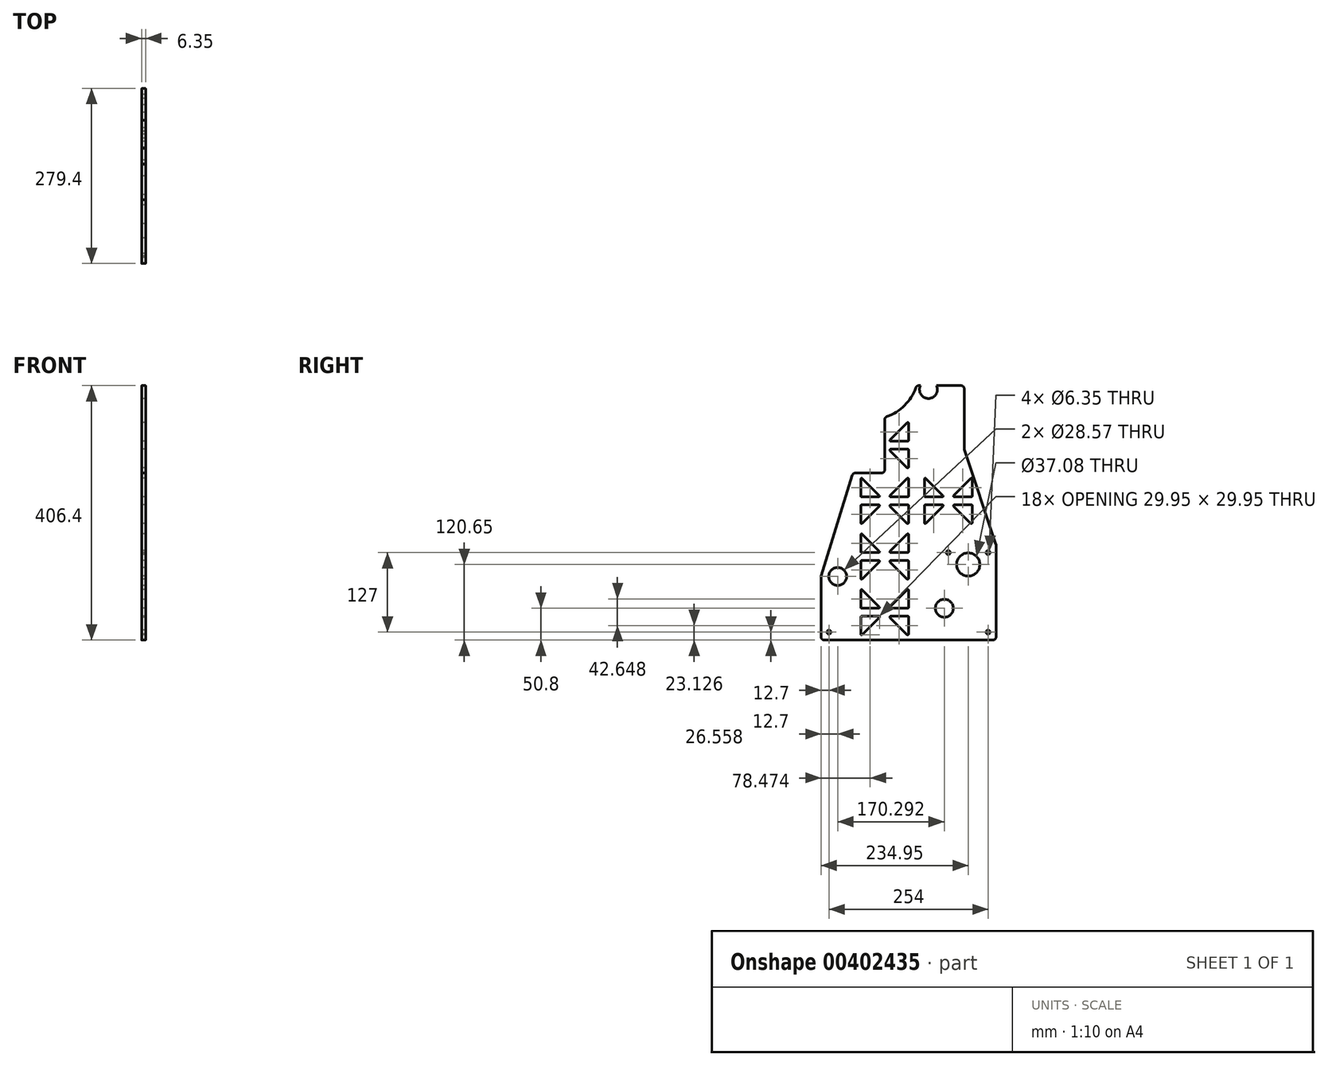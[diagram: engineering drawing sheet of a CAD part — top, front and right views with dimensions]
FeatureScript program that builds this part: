
annotation { "Feature Type Name" : "Feature", "Feature Type Description" : "" }
export const myFeature = defineFeature(function(context is Context, id is Id, definition is map)
    precondition{}
    {
        {
            var Q0;
            Q0=qCreatedBy(makeId("Right.planeOp"),FACE);
            var sketch = newSketch(context, id + "F0", { "sketchPlane" : qUnion([Q0])});
            skLineSegment(sketch, "E0.bottom", {"start": v(0, 0) * mm, "end": v(101.6, 0) * mm});
            skLineSegment(sketch, "E0.top", {"start": v(0, 406.4) * mm, "end": v(101.6, 406.4) * mm});
            skLineSegment(sketch, "E0.left", {"start": v(0, 0) * mm, "end": v(0, 406.4) * mm});
            skLineSegment(sketch, "E0.right", {"start": v(101.6, 0) * mm, "end": v(101.6, 406.4) * mm});
            skLineSegment(sketch, "E1.bottom", {"start": v(101.6, 0) * mm, "end": v(228.6, 0) * mm});
            skLineSegment(sketch, "E1.top", {"start": v(101.6, 152.4) * mm, "end": v(228.6, 152.4) * mm});
            skLineSegment(sketch, "E1.left", {"start": v(101.6, 0) * mm, "end": v(101.6, 152.4) * mm});
            skLineSegment(sketch, "E1.right", {"start": v(228.6, 0) * mm, "end": v(228.6, 152.4) * mm});
            skCircle(sketch, "E2", {"center": v(146.05, 50.8) * mm, "radius": 14.29 * mm});
            skCircle(sketch, "E3", {"center": v(146.05, 50.8) * mm, "radius": 50.8 * mm, "construction": true});
            skCircle(sketch, "E4", {"center": v(184.15, 120.65) * mm, "radius": 18.54 * mm});
            skCircle(sketch, "E5", {"center": v(215.9, 12.7) * mm, "radius": 3.18 * mm});
            skCircle(sketch, "E6", {"center": v(215.9, 139.7) * mm, "radius": 3.18 * mm});
            skPoint(sketch, "E7.startSnap0", {"position": v(50.8, 406.4) * mm});
            skLineSegment(sketch, "E8", {"start": v(50.8, 406.4) * mm, "end": v(50.8, -18.77) * mm, "construction": true});
            skPoint(sketch, "E8.endSnap0", {"position": v(50.8, 0) * mm});
            skArc(sketch, "E9.MirrorCS", {"start": v(12.7, 392.43) * mm, "mid": v(13.07, 393.33) * mm, "end": v(13.97, 393.7) * mm});
            skArc(sketch, "E10.MirrorCS", {"start": v(41.38, 393.7) * mm, "mid": v(42.56, 392.92) * mm, "end": v(42.28, 391.53) * mm});
            skPoint(sketch, "E11.MirrorP", {"position": v(12.7, 361.95) * mm});
            skLineSegment(sketch, "E12.MirrorCS", {"start": v(13.97, 393.7) * mm, "end": v(41.38, 393.7) * mm});
            skPoint(sketch, "E13.MirrorP", {"position": v(12.7, 393.7) * mm});
            skLineSegment(sketch, "E14.MirrorCS", {"start": v(42.28, 391.53) * mm, "end": v(14.87, 364.12) * mm});
            skPoint(sketch, "E15.MirrorP", {"position": v(44.45, 393.7) * mm});
            skArc(sketch, "E16.MirrorCS", {"start": v(14.87, 364.12) * mm, "mid": v(13.48, 363.84) * mm, "end": v(12.7, 365.02) * mm});
            skLineSegment(sketch, "E17.MirrorCS", {"start": v(12.7, 365.02) * mm, "end": v(12.7, 392.43) * mm});
            skLineSegment(sketch, "E18", {"start": v(-14.42, 355.6) * mm, "end": v(137.53, 355.6) * mm, "construction": true});
            skArc(sketch, "E19.MirrorCS", {"start": v(12.7, 318.77) * mm, "mid": v(13.07, 317.87) * mm, "end": v(13.97, 317.5) * mm});
            skArc(sketch, "E20.MirrorCS", {"start": v(60.22, 317.5) * mm, "mid": v(59.04, 318.28) * mm, "end": v(59.32, 319.67) * mm});
            skArc(sketch, "E21.MirrorCS", {"start": v(14.87, 347.08) * mm, "mid": v(13.48, 347.36) * mm, "end": v(12.7, 346.18) * mm});
            skArc(sketch, "E22.MirrorCS", {"start": v(41.38, 317.5) * mm, "mid": v(42.56, 318.28) * mm, "end": v(42.28, 319.67) * mm});
            skArc(sketch, "E23.MirrorCS", {"start": v(86.73, 347.08) * mm, "mid": v(88.12, 347.36) * mm, "end": v(88.9, 346.18) * mm});
            skArc(sketch, "E24.MirrorCS", {"start": v(88.9, 318.77) * mm, "mid": v(88.53, 317.87) * mm, "end": v(87.63, 317.5) * mm});
            skPoint(sketch, "E25.MirrorP", {"position": v(12.7, 349.25) * mm});
            skPoint(sketch, "E26.MirrorP", {"position": v(88.9, 349.25) * mm});
            skPoint(sketch, "E27.MirrorP", {"position": v(12.7, 317.5) * mm});
            skPoint(sketch, "E28.MirrorP", {"position": v(44.45, 317.5) * mm});
            skLineSegment(sketch, "E29.MirrorCS", {"start": v(50.8, 304.8) * mm, "end": v(50.8, 729.97) * mm, "construction": true});
            skPoint(sketch, "E30.MirrorP", {"position": v(88.9, 317.5) * mm});
            skLineSegment(sketch, "E31.MirrorCS", {"start": v(12.7, 346.18) * mm, "end": v(12.7, 318.77) * mm});
            skLineSegment(sketch, "E32.MirrorCS", {"start": v(88.9, 346.18) * mm, "end": v(88.9, 318.77) * mm});
            skLineSegment(sketch, "E33.MirrorCS", {"start": v(42.28, 319.67) * mm, "end": v(14.87, 347.08) * mm});
            skLineSegment(sketch, "E34.MirrorCS", {"start": v(13.97, 317.5) * mm, "end": v(41.38, 317.5) * mm});
            skPoint(sketch, "E35.MirrorP", {"position": v(57.15, 317.5) * mm});
            skLineSegment(sketch, "E36.MirrorCS", {"start": v(87.63, 317.5) * mm, "end": v(60.22, 317.5) * mm});
            skLineSegment(sketch, "E37.MirrorCS", {"start": v(59.32, 319.67) * mm, "end": v(86.73, 347.08) * mm});
            skPoint(sketch, "E38.0.1.0", {"position": v(44.45, 304.8) * mm});
            skLineSegment(sketch, "E38.0.1.1", {"start": v(12.7, 276.12) * mm, "end": v(12.7, 303.53) * mm});
            skPoint(sketch, "E38.0.1.2", {"position": v(12.7, 273.05) * mm});
            skPoint(sketch, "E38.0.1.3", {"position": v(12.7, 304.8) * mm});
            skLineSegment(sketch, "E38.0.1.4", {"start": v(42.28, 302.63) * mm, "end": v(14.87, 275.22) * mm});
            skLineSegment(sketch, "E38.0.1.5", {"start": v(13.97, 304.8) * mm, "end": v(41.38, 304.8) * mm});
            skPoint(sketch, "E38.0.1.6", {"position": v(12.7, 273.05) * mm});
            skArc(sketch, "E38.0.1.7", {"start": v(14.87, 275.22) * mm, "mid": v(13.48, 274.94) * mm, "end": v(12.7, 276.12) * mm});
            skArc(sketch, "E38.0.1.8", {"start": v(41.38, 304.8) * mm, "mid": v(42.56, 304.02) * mm, "end": v(42.28, 302.63) * mm});
            skArc(sketch, "E38.0.1.9", {"start": v(12.7, 303.53) * mm, "mid": v(13.07, 304.43) * mm, "end": v(13.97, 304.8) * mm});
            skPoint(sketch, "E38.0.1.10", {"position": v(44.45, 228.6) * mm});
            skLineSegment(sketch, "E38.0.1.11", {"start": v(13.97, 228.6) * mm, "end": v(41.38, 228.6) * mm});
            skPoint(sketch, "E38.0.1.12", {"position": v(12.7, 260.35) * mm});
            skLineSegment(sketch, "E38.0.1.13", {"start": v(42.28, 230.77) * mm, "end": v(14.87, 258.18) * mm});
            skPoint(sketch, "E38.0.1.14", {"position": v(12.7, 228.6) * mm});
            skLineSegment(sketch, "E38.0.1.15", {"start": v(12.7, 257.28) * mm, "end": v(12.7, 229.87) * mm});
            skPoint(sketch, "E38.0.1.16", {"position": v(12.7, 260.35) * mm});
            skArc(sketch, "E38.0.1.17", {"start": v(41.38, 228.6) * mm, "mid": v(42.56, 229.38) * mm, "end": v(42.28, 230.77) * mm});
            skArc(sketch, "E38.0.1.18", {"start": v(14.87, 258.18) * mm, "mid": v(13.48, 258.46) * mm, "end": v(12.7, 257.28) * mm});
            skArc(sketch, "E38.0.1.19", {"start": v(12.7, 229.87) * mm, "mid": v(13.07, 228.97) * mm, "end": v(13.97, 228.6) * mm});
            skPoint(sketch, "E38.0.1.20", {"position": v(57.15, 228.6) * mm});
            skPoint(sketch, "E38.0.1.21", {"position": v(88.9, 228.6) * mm});
            skLineSegment(sketch, "E38.0.1.22", {"start": v(59.32, 230.77) * mm, "end": v(86.73, 258.18) * mm});
            skLineSegment(sketch, "E38.0.1.23", {"start": v(87.63, 228.6) * mm, "end": v(60.22, 228.6) * mm});
            skPoint(sketch, "E38.0.1.24", {"position": v(88.9, 260.35) * mm});
            skLineSegment(sketch, "E38.0.1.25", {"start": v(88.9, 257.28) * mm, "end": v(88.9, 229.87) * mm});
            skPoint(sketch, "E38.0.1.26", {"position": v(88.9, 260.35) * mm});
            skArc(sketch, "E38.0.1.27", {"start": v(60.22, 228.6) * mm, "mid": v(59.04, 229.38) * mm, "end": v(59.32, 230.77) * mm});
            skArc(sketch, "E38.0.1.28", {"start": v(88.9, 229.87) * mm, "mid": v(88.53, 228.97) * mm, "end": v(87.63, 228.6) * mm});
            skArc(sketch, "E38.0.1.29", {"start": v(86.73, 258.18) * mm, "mid": v(88.12, 258.46) * mm, "end": v(88.9, 257.28) * mm});
            skLineSegment(sketch, "E38.0.1.30", {"start": v(88.9, 276.12) * mm, "end": v(88.9, 303.53) * mm});
            skLineSegment(sketch, "E38.0.1.31", {"start": v(59.32, 302.63) * mm, "end": v(86.73, 275.22) * mm});
            skLineSegment(sketch, "E38.0.1.32", {"start": v(87.63, 304.8) * mm, "end": v(60.22, 304.8) * mm});
            skPoint(sketch, "E38.0.1.33", {"position": v(88.9, 304.8) * mm});
            skPoint(sketch, "E38.0.1.34", {"position": v(88.9, 273.05) * mm});
            skPoint(sketch, "E38.0.1.35", {"position": v(57.15, 304.8) * mm});
            skPoint(sketch, "E38.0.1.36", {"position": v(88.9, 273.05) * mm});
            skArc(sketch, "E38.0.1.37", {"start": v(86.73, 275.22) * mm, "mid": v(88.12, 274.94) * mm, "end": v(88.9, 276.12) * mm});
            skArc(sketch, "E38.0.1.38", {"start": v(88.9, 303.53) * mm, "mid": v(88.53, 304.43) * mm, "end": v(87.63, 304.8) * mm});
            skArc(sketch, "E38.0.1.39", {"start": v(60.22, 304.8) * mm, "mid": v(59.04, 304.02) * mm, "end": v(59.32, 302.63) * mm});
            skPoint(sketch, "E38.0.2.0", {"position": v(44.45, 215.9) * mm});
            skLineSegment(sketch, "E38.0.2.1", {"start": v(12.7, 187.22) * mm, "end": v(12.7, 214.63) * mm});
            skPoint(sketch, "E38.0.2.2", {"position": v(12.7, 184.15) * mm});
            skPoint(sketch, "E38.0.2.3", {"position": v(12.7, 215.9) * mm});
            skLineSegment(sketch, "E38.0.2.4", {"start": v(42.28, 213.73) * mm, "end": v(14.87, 186.32) * mm});
            skLineSegment(sketch, "E38.0.2.5", {"start": v(13.97, 215.9) * mm, "end": v(41.38, 215.9) * mm});
            skPoint(sketch, "E38.0.2.6", {"position": v(12.7, 184.15) * mm});
            skArc(sketch, "E38.0.2.7", {"start": v(14.87, 186.32) * mm, "mid": v(13.48, 186.04) * mm, "end": v(12.7, 187.22) * mm});
            skArc(sketch, "E38.0.2.8", {"start": v(41.38, 215.9) * mm, "mid": v(42.56, 215.12) * mm, "end": v(42.28, 213.73) * mm});
            skArc(sketch, "E38.0.2.9", {"start": v(12.7, 214.63) * mm, "mid": v(13.07, 215.53) * mm, "end": v(13.97, 215.9) * mm});
            skPoint(sketch, "E38.0.2.10", {"position": v(44.45, 139.7) * mm});
            skLineSegment(sketch, "E38.0.2.11", {"start": v(13.97, 139.7) * mm, "end": v(41.38, 139.7) * mm});
            skPoint(sketch, "E38.0.2.12", {"position": v(12.7, 171.45) * mm});
            skLineSegment(sketch, "E38.0.2.13", {"start": v(42.28, 141.87) * mm, "end": v(14.87, 169.28) * mm});
            skPoint(sketch, "E38.0.2.14", {"position": v(12.7, 139.7) * mm});
            skLineSegment(sketch, "E38.0.2.15", {"start": v(12.7, 168.38) * mm, "end": v(12.7, 140.97) * mm});
            skPoint(sketch, "E38.0.2.16", {"position": v(12.7, 171.45) * mm});
            skArc(sketch, "E38.0.2.17", {"start": v(41.38, 139.7) * mm, "mid": v(42.56, 140.48) * mm, "end": v(42.28, 141.87) * mm});
            skArc(sketch, "E38.0.2.18", {"start": v(14.87, 169.28) * mm, "mid": v(13.48, 169.56) * mm, "end": v(12.7, 168.38) * mm});
            skArc(sketch, "E38.0.2.19", {"start": v(12.7, 140.97) * mm, "mid": v(13.07, 140.07) * mm, "end": v(13.97, 139.7) * mm});
            skPoint(sketch, "E38.0.2.20", {"position": v(57.15, 139.7) * mm});
            skPoint(sketch, "E38.0.2.21", {"position": v(88.9, 139.7) * mm});
            skLineSegment(sketch, "E38.0.2.22", {"start": v(59.32, 141.87) * mm, "end": v(86.73, 169.28) * mm});
            skLineSegment(sketch, "E38.0.2.23", {"start": v(87.63, 139.7) * mm, "end": v(60.22, 139.7) * mm});
            skPoint(sketch, "E38.0.2.24", {"position": v(88.9, 171.45) * mm});
            skLineSegment(sketch, "E38.0.2.25", {"start": v(88.9, 168.38) * mm, "end": v(88.9, 140.97) * mm});
            skPoint(sketch, "E38.0.2.26", {"position": v(88.9, 171.45) * mm});
            skArc(sketch, "E38.0.2.27", {"start": v(60.22, 139.7) * mm, "mid": v(59.04, 140.48) * mm, "end": v(59.32, 141.87) * mm});
            skArc(sketch, "E38.0.2.28", {"start": v(88.9, 140.97) * mm, "mid": v(88.53, 140.07) * mm, "end": v(87.63, 139.7) * mm});
            skArc(sketch, "E38.0.2.29", {"start": v(86.73, 169.28) * mm, "mid": v(88.12, 169.56) * mm, "end": v(88.9, 168.38) * mm});
            skLineSegment(sketch, "E38.0.2.30", {"start": v(88.9, 187.22) * mm, "end": v(88.9, 214.63) * mm});
            skLineSegment(sketch, "E38.0.2.31", {"start": v(59.32, 213.73) * mm, "end": v(86.73, 186.32) * mm});
            skLineSegment(sketch, "E38.0.2.32", {"start": v(87.63, 215.9) * mm, "end": v(60.22, 215.9) * mm});
            skPoint(sketch, "E38.0.2.33", {"position": v(88.9, 215.9) * mm});
            skPoint(sketch, "E38.0.2.34", {"position": v(88.9, 184.15) * mm});
            skPoint(sketch, "E38.0.2.35", {"position": v(57.15, 215.9) * mm});
            skPoint(sketch, "E38.0.2.36", {"position": v(88.9, 184.15) * mm});
            skArc(sketch, "E38.0.2.37", {"start": v(86.73, 186.32) * mm, "mid": v(88.12, 186.04) * mm, "end": v(88.9, 187.22) * mm});
            skArc(sketch, "E38.0.2.38", {"start": v(88.9, 214.63) * mm, "mid": v(88.53, 215.53) * mm, "end": v(87.63, 215.9) * mm});
            skArc(sketch, "E38.0.2.39", {"start": v(60.22, 215.9) * mm, "mid": v(59.04, 215.12) * mm, "end": v(59.32, 213.73) * mm});
            skLineSegment(sketch, "E38.direction1", {"start": v(12.7, 317.5) * mm, "end": v(12.65, 317.5) * mm, "construction": true});
            skLineSegment(sketch, "E38.direction2", {"start": v(12.7, 317.5) * mm, "end": v(12.7, 228.6) * mm, "construction": true});
            skPoint(sketch, "E39.25.0.3", {"position": v(44.45, 50.8) * mm});
            skLineSegment(sketch, "E39.26.0.3", {"start": v(13.97, 50.8) * mm, "end": v(41.38, 50.8) * mm});
            skPoint(sketch, "E39.29.0.3", {"position": v(12.7, 82.55) * mm});
            skLineSegment(sketch, "E39.30.0.3", {"start": v(42.28, 52.97) * mm, "end": v(14.87, 80.38) * mm});
            skPoint(sketch, "E39.33.0.3", {"position": v(12.7, 50.8) * mm});
            skLineSegment(sketch, "E39.34.0.3", {"start": v(12.7, 79.48) * mm, "end": v(12.7, 52.07) * mm});
            skPoint(sketch, "E39.37.0.3", {"position": v(12.7, 82.55) * mm});
            skArc(sketch, "E39.38.0.3", {"start": v(41.38, 50.8) * mm, "mid": v(42.56, 51.58) * mm, "end": v(42.28, 52.97) * mm});
            skArc(sketch, "E39.42.0.3", {"start": v(14.87, 80.38) * mm, "mid": v(13.48, 80.66) * mm, "end": v(12.7, 79.48) * mm});
            skArc(sketch, "E39.46.0.3", {"start": v(12.7, 52.07) * mm, "mid": v(13.07, 51.17) * mm, "end": v(13.97, 50.8) * mm});
            skPoint(sketch, "E39.50.0.3", {"position": v(57.15, 50.8) * mm});
            skPoint(sketch, "E39.51.0.3", {"position": v(88.9, 50.8) * mm});
            skLineSegment(sketch, "E39.52.0.3", {"start": v(59.32, 52.97) * mm, "end": v(86.73, 80.38) * mm});
            skLineSegment(sketch, "E39.55.0.3", {"start": v(87.63, 50.8) * mm, "end": v(60.22, 50.8) * mm});
            skPoint(sketch, "E39.58.0.3", {"position": v(88.9, 82.55) * mm});
            skLineSegment(sketch, "E39.59.0.3", {"start": v(88.9, 79.48) * mm, "end": v(88.9, 52.07) * mm});
            skPoint(sketch, "E39.62.0.3", {"position": v(88.9, 82.55) * mm});
            skArc(sketch, "E39.63.0.3", {"start": v(60.22, 50.8) * mm, "mid": v(59.04, 51.58) * mm, "end": v(59.32, 52.97) * mm});
            skArc(sketch, "E39.67.0.3", {"start": v(88.9, 52.07) * mm, "mid": v(88.53, 51.17) * mm, "end": v(87.63, 50.8) * mm});
            skArc(sketch, "E39.71.0.3", {"start": v(86.73, 80.38) * mm, "mid": v(88.12, 80.66) * mm, "end": v(88.9, 79.48) * mm});
            skLineSegment(sketch, "E39.75.0.3", {"start": v(88.9, 98.32) * mm, "end": v(88.9, 125.73) * mm});
            skLineSegment(sketch, "E39.78.0.3", {"start": v(59.32, 124.83) * mm, "end": v(86.73, 97.42) * mm});
            skLineSegment(sketch, "E39.81.0.3", {"start": v(87.63, 127) * mm, "end": v(60.22, 127) * mm});
            skPoint(sketch, "E39.84.0.3", {"position": v(88.9, 127) * mm});
            skPoint(sketch, "E39.85.0.3", {"position": v(88.9, 95.25) * mm});
            skPoint(sketch, "E39.86.0.3", {"position": v(57.15, 127) * mm});
            skPoint(sketch, "E39.87.0.3", {"position": v(88.9, 95.25) * mm});
            skArc(sketch, "E39.88.0.3", {"start": v(86.73, 97.42) * mm, "mid": v(88.12, 97.14) * mm, "end": v(88.9, 98.32) * mm});
            skArc(sketch, "E39.92.0.3", {"start": v(88.9, 125.73) * mm, "mid": v(88.53, 126.63) * mm, "end": v(87.63, 127) * mm});
            skArc(sketch, "E39.96.0.3", {"start": v(60.22, 127) * mm, "mid": v(59.04, 126.22) * mm, "end": v(59.32, 124.83) * mm});
            skPoint(sketch, "E39.0.0.4", {"position": v(44.45, 38.1) * mm});
            skLineSegment(sketch, "E39.1.0.4", {"start": v(12.7, 9.42) * mm, "end": v(12.7, 36.83) * mm});
            skPoint(sketch, "E39.4.0.4", {"position": v(12.7, 6.35) * mm});
            skPoint(sketch, "E39.5.0.4", {"position": v(12.7, 38.1) * mm});
            skLineSegment(sketch, "E39.6.0.4", {"start": v(42.28, 35.93) * mm, "end": v(14.87, 8.52) * mm});
            skLineSegment(sketch, "E39.9.0.4", {"start": v(13.97, 38.1) * mm, "end": v(41.38, 38.1) * mm});
            skPoint(sketch, "E39.12.0.4", {"position": v(12.7, 6.35) * mm});
            skArc(sketch, "E39.13.0.4", {"start": v(14.87, 8.52) * mm, "mid": v(13.48, 8.24) * mm, "end": v(12.7, 9.42) * mm});
            skArc(sketch, "E39.17.0.4", {"start": v(41.38, 38.1) * mm, "mid": v(42.56, 37.32) * mm, "end": v(42.28, 35.93) * mm});
            skArc(sketch, "E39.21.0.4", {"start": v(12.7, 36.83) * mm, "mid": v(13.07, 37.73) * mm, "end": v(13.97, 38.1) * mm});
            skLineSegment(sketch, "E39.75.0.4", {"start": v(88.9, 9.42) * mm, "end": v(88.9, 36.83) * mm});
            skLineSegment(sketch, "E39.78.0.4", {"start": v(59.32, 35.93) * mm, "end": v(86.73, 8.52) * mm});
            skLineSegment(sketch, "E39.81.0.4", {"start": v(87.63, 38.1) * mm, "end": v(60.22, 38.1) * mm});
            skPoint(sketch, "E39.84.0.4", {"position": v(88.9, 38.1) * mm});
            skPoint(sketch, "E39.85.0.4", {"position": v(88.9, 6.35) * mm});
            skPoint(sketch, "E39.86.0.4", {"position": v(57.15, 38.1) * mm});
            skPoint(sketch, "E39.87.0.4", {"position": v(88.9, 6.35) * mm});
            skArc(sketch, "E39.88.0.4", {"start": v(86.73, 8.52) * mm, "mid": v(88.12, 8.24) * mm, "end": v(88.9, 9.42) * mm});
            skArc(sketch, "E39.92.0.4", {"start": v(88.9, 36.83) * mm, "mid": v(88.53, 37.73) * mm, "end": v(87.63, 38.1) * mm});
            skArc(sketch, "E39.96.0.4", {"start": v(60.22, 38.1) * mm, "mid": v(59.04, 37.32) * mm, "end": v(59.32, 35.93) * mm});
            skArc(sketch, "E40", {"start": v(101.6, 190.5) * mm, "mid": v(112.76, 163.56) * mm, "end": v(139.7, 152.4) * mm});
            skLineSegment(sketch, "E41", {"start": v(139.7, 190.5) * mm, "end": v(101.6, 190.5) * mm});
            skCircle(sketch, "E42", {"center": v(215.9, 139.7) * mm, "radius": 6.35 * mm, "construction": true});
            skCircle(sketch, "E43", {"center": v(152.4, 139.7) * mm, "radius": 3.18 * mm});
            skCircle(sketch, "E44", {"center": v(152.4, 139.7) * mm, "radius": 6.35 * mm, "construction": true});
            skCircle(sketch, "E45", {"center": v(215.9, 12.7) * mm, "radius": 6.35 * mm, "construction": true});
            skLineSegment(sketch, "E46.bottom", {"start": v(0, 266.7) * mm, "end": v(50.8, 266.7) * mm});
            skLineSegment(sketch, "E46.top", {"start": v(0, 406.4) * mm, "end": v(50.8, 406.4) * mm});
            skLineSegment(sketch, "E46.left", {"start": v(0, 266.7) * mm, "end": v(0, 406.4) * mm});
            skLineSegment(sketch, "E46.right", {"start": v(50.8, 266.7) * mm, "end": v(50.8, 406.4) * mm});
            skLineSegment(sketch, "E47.bottom", {"start": v(0, 266.7) * mm, "end": v(-50.8, 266.7) * mm});
            skLineSegment(sketch, "E47.top", {"start": v(0, 0) * mm, "end": v(-50.8, 0) * mm});
            skLineSegment(sketch, "E47.left", {"start": v(0, 266.7) * mm, "end": v(0, 0) * mm});
            skLineSegment(sketch, "E47.right", {"start": v(-50.8, 266.7) * mm, "end": v(-50.8, 0) * mm});
            skCircle(sketch, "E48", {"center": v(-24.24, 101.6) * mm, "radius": 14.29 * mm});
            skLineSegment(sketch, "E49", {"start": v(0, 266.7) * mm, "end": v(-50.8, 101.6) * mm});
            skLineSegment(sketch, "E50.bottom", {"start": v(101.6, 304.8) * mm, "end": v(177.8, 304.8) * mm});
            skLineSegment(sketch, "E50.top", {"start": v(101.6, 406.4) * mm, "end": v(177.8, 406.4) * mm});
            skLineSegment(sketch, "E50.left", {"start": v(101.6, 304.8) * mm, "end": v(101.6, 406.4) * mm});
            skLineSegment(sketch, "E50.right", {"start": v(177.8, 304.8) * mm, "end": v(177.8, 406.4) * mm});
            skLineSegment(sketch, "E51.bottom", {"start": v(177.8, 406.4) * mm, "end": v(101.6, 406.4) * mm});
            skLineSegment(sketch, "E51.top", {"start": v(177.8, 419.1) * mm, "end": v(101.6, 419.1) * mm});
            skLineSegment(sketch, "E51.left", {"start": v(177.8, 406.4) * mm, "end": v(177.8, 419.1) * mm});
            skLineSegment(sketch, "E51.right", {"start": v(101.6, 406.4) * mm, "end": v(101.6, 419.1) * mm});
            skCircle(sketch, "E52", {"center": v(120.65, 400.05) * mm, "radius": 14.29 * mm});
            skCircle(sketch, "E53", {"center": v(-38.1, 12.7) * mm, "radius": 3.18 * mm});
            skLineSegment(sketch, "E54", {"start": v(228.6, 152.4) * mm, "end": v(177.8, 304.8) * mm});
            skArc(sketch, "E55.MirrorCS", {"start": v(190.5, 229.87) * mm, "mid": v(190.13, 228.97) * mm, "end": v(189.23, 228.6) * mm});
            skArc(sketch, "E56.MirrorCS", {"start": v(190.5, 214.63) * mm, "mid": v(190.13, 215.53) * mm, "end": v(189.23, 215.9) * mm});
            skArc(sketch, "E57.MirrorCS", {"start": v(116.47, 186.32) * mm, "mid": v(115.08, 186.04) * mm, "end": v(114.3, 187.22) * mm});
            skArc(sketch, "E58.MirrorCS", {"start": v(114.3, 214.63) * mm, "mid": v(114.67, 215.53) * mm, "end": v(115.57, 215.9) * mm});
            skArc(sketch, "E59.MirrorCS", {"start": v(114.3, 229.87) * mm, "mid": v(114.67, 228.97) * mm, "end": v(115.57, 228.6) * mm});
            skArc(sketch, "E60.MirrorCS", {"start": v(188.33, 258.18) * mm, "mid": v(189.72, 258.46) * mm, "end": v(190.5, 257.28) * mm});
            skArc(sketch, "E61.MirrorCS", {"start": v(161.82, 215.9) * mm, "mid": v(160.64, 215.12) * mm, "end": v(160.92, 213.73) * mm});
            skArc(sketch, "E62.MirrorCS", {"start": v(142.98, 228.6) * mm, "mid": v(144.16, 229.38) * mm, "end": v(143.88, 230.77) * mm});
            skArc(sketch, "E63.MirrorCS", {"start": v(188.33, 186.32) * mm, "mid": v(189.72, 186.04) * mm, "end": v(190.5, 187.22) * mm});
            skArc(sketch, "E64.MirrorCS", {"start": v(116.47, 258.18) * mm, "mid": v(115.08, 258.46) * mm, "end": v(114.3, 257.28) * mm});
            skArc(sketch, "E65.MirrorCS", {"start": v(142.98, 215.9) * mm, "mid": v(144.16, 215.12) * mm, "end": v(143.88, 213.73) * mm});
            skArc(sketch, "E66.MirrorCS", {"start": v(161.82, 228.6) * mm, "mid": v(160.64, 229.38) * mm, "end": v(160.92, 230.77) * mm});
            skPoint(sketch, "E67.MirrorP", {"position": v(190.5, 184.15) * mm});
            skPoint(sketch, "E68.MirrorP", {"position": v(114.3, 184.15) * mm});
            skPoint(sketch, "E69.MirrorP", {"position": v(114.3, 260.35) * mm});
            skPoint(sketch, "E70.MirrorP", {"position": v(190.5, 260.35) * mm});
            skLineSegment(sketch, "E71.MirrorCS", {"start": v(189.23, 215.9) * mm, "end": v(161.82, 215.9) * mm});
            skLineSegment(sketch, "E72.MirrorCS", {"start": v(114.3, 187.22) * mm, "end": v(114.3, 214.63) * mm});
            skLineSegment(sketch, "E73.MirrorCS", {"start": v(115.57, 215.9) * mm, "end": v(142.98, 215.9) * mm});
            skPoint(sketch, "E74.MirrorP", {"position": v(146.05, 215.9) * mm});
            skPoint(sketch, "E75.MirrorP", {"position": v(190.5, 215.9) * mm});
            skPoint(sketch, "E76.MirrorP", {"position": v(146.05, 228.6) * mm});
            skLineSegment(sketch, "E77.MirrorCS", {"start": v(190.5, 187.22) * mm, "end": v(190.5, 214.63) * mm});
            skLineSegment(sketch, "E78.MirrorCS", {"start": v(160.92, 213.73) * mm, "end": v(188.33, 186.32) * mm});
            skLineSegment(sketch, "E79.MirrorCS", {"start": v(143.88, 213.73) * mm, "end": v(116.47, 186.32) * mm});
            skLineSegment(sketch, "E80.MirrorCS", {"start": v(143.88, 230.77) * mm, "end": v(116.47, 258.18) * mm});
            skPoint(sketch, "E81.MirrorP", {"position": v(190.5, 228.6) * mm});
            skPoint(sketch, "E82.MirrorP", {"position": v(158.75, 215.9) * mm});
            skLineSegment(sketch, "E83.MirrorCS", {"start": v(160.92, 230.77) * mm, "end": v(188.33, 258.18) * mm});
            skPoint(sketch, "E84.MirrorP", {"position": v(114.3, 215.9) * mm});
            skPoint(sketch, "E85.MirrorP", {"position": v(114.3, 228.6) * mm});
            skLineSegment(sketch, "E86.MirrorCS", {"start": v(190.5, 257.28) * mm, "end": v(190.5, 229.87) * mm});
            skLineSegment(sketch, "E87.MirrorCS", {"start": v(115.57, 228.6) * mm, "end": v(142.98, 228.6) * mm});
            skLineSegment(sketch, "E88.MirrorCS", {"start": v(189.23, 228.6) * mm, "end": v(161.82, 228.6) * mm});
            skLineSegment(sketch, "E89.MirrorCS", {"start": v(114.3, 257.28) * mm, "end": v(114.3, 229.87) * mm});
            skPoint(sketch, "E90.MirrorP", {"position": v(158.75, 228.6) * mm});
            skArc(sketch, "E91.MirrorCS", {"start": v(12.7, 125.73) * mm, "mid": v(13.07, 126.63) * mm, "end": v(13.97, 127) * mm});
            skArc(sketch, "E92.MirrorCS", {"start": v(14.87, 97.42) * mm, "mid": v(13.48, 97.14) * mm, "end": v(12.7, 98.32) * mm});
            skArc(sketch, "E93.MirrorCS", {"start": v(41.38, 127) * mm, "mid": v(42.56, 126.22) * mm, "end": v(42.28, 124.83) * mm});
            skPoint(sketch, "E94.MirrorP", {"position": v(12.7, 95.25) * mm});
            skPoint(sketch, "E95.MirrorP", {"position": v(44.45, 127) * mm});
            skLineSegment(sketch, "E96.MirrorCS", {"start": v(13.97, 127) * mm, "end": v(41.38, 127) * mm});
            skPoint(sketch, "E97.MirrorP", {"position": v(12.7, 127) * mm});
            skLineSegment(sketch, "E98.MirrorCS", {"start": v(42.28, 124.83) * mm, "end": v(14.87, 97.42) * mm});
            skLineSegment(sketch, "E99.MirrorCS", {"start": v(12.7, 98.32) * mm, "end": v(12.7, 125.73) * mm});
            skArc(sketch, "E100", {"start": v(50.8, 355.6) * mm, "mid": v(82.56, 374.64) * mm, "end": v(101.6, 406.4) * mm});
            skSolve(sketch);
        }
        {
            var Q0;
            Q0=makeQuery(id+"F0.imprint","IMPRINT",FACE,{"disambiguationData":[TD([[makeQuery(id+"F0.imprint","IMPRINT",EDGE,{"derivedFrom":sQuery(id+"F0.wireOp",EDGE,"E0.bottom")}),1.0]])]});
            var Q1;
            Q1=makeQuery(id+"F0.imprint","IMPRINT",FACE,{"disambiguationData":[TD([[makeQuery(id+"F0.imprint","IMPRINT",EDGE,{"derivedFrom":sQuery(id+"F0.wireOp",EDGE,"E1.bottom")}),1.0]])]});
            var Q2;
            {var subQ3=sQuery(id+"F0.wireOp",EDGE,"E40");Q2=makeQuery(id+"F0.imprint","IMPRINT",FACE,{"disambiguationData":[TD([[makeQuery(id+"F0.imprint","IMPRINT",EDGE,{"derivedFrom":subQ3}),-1.0]])]});}
            var Q3;
            {var subQ1=sQuery(id+"F0.wireOp",EDGE,"E47.top");Q3=makeQuery(id+"F0.imprint","IMPRINT",FACE,{"disambiguationData":[TD([[makeQuery(id+"F0.imprint","IMPRINT",EDGE,{"derivedFrom":subQ1}),-1.0]])]});}
            var Q4;
            Q4=makeQuery(id+"F0.imprint","IMPRINT",FACE,{"disambiguationData":[TD([[makeQuery(id+"F0.imprint","IMPRINT",EDGE,{"derivedFrom":sQuery(id+"F0.wireOp",EDGE,"E50.bottom")}),1.0]])]});
            var Q5;
            Q5=makeQuery(id+"F0.imprint","IMPRINT",FACE,{"disambiguationData":[TD([[makeQuery(id+"F0.imprint","IMPRINT",EDGE,{"derivedFrom":sQuery(id+"F0.wireOp",EDGE,"E51.bottom")}),-1.0]])]});
            var Q6;
            {var subQ0=sQuery(id+"F0.wireOp",EDGE,"E40");Q6=makeQuery(id+"F0.imprint","IMPRINT",FACE,{"disambiguationData":[TD([[makeQuery(id+"F0.imprint","IMPRINT",EDGE,{"derivedFrom":subQ0}),1.0]])]});}
            extrude(context, id + "F1", {"entities" : qUnion([Q0, Q1, Q2, Q3, Q4, Q5, Q6]), "depth" : 6.35 * mm});
        }
        {
            var Q0;
            Q0=makeQuery(id+"F1.opExtrude","SWEPT_EDGE",EDGE,{"disambiguationData":[OSD([sQuery(id+"F0.wireOp",EDGE,"E0.top"),sQuery(id+"F0.wireOp",EDGE,"E50.left"),sQuery(id+"F0.wireOp",EDGE,"E51.bottom"),sQuery(id+"F0.wireOp",EDGE,"E51.right")])]});
            var Q1;
            Q1=makeQuery(id+"F1.opExtrude","SWEPT_EDGE",EDGE,{"disambiguationData":[OSD([sQuery(id+"F0.wireOp",EDGE,"E51.top"),sQuery(id+"F0.wireOp",EDGE,"E51.right")])]});
            var Q2;
            Q2=makeQuery(id+"F1.opExtrude","SWEPT_EDGE",EDGE,{"disambiguationData":[OSD([sQuery(id+"F0.wireOp",EDGE,"E51.top"),sQuery(id+"F0.wireOp",EDGE,"E51.left")])]});
            fillet(context, id + "F2", {"entities" : qUnion([Q0, Q1, Q2]), "radius" : 5.08 * mm, "tangentPropagation" : true, "allowEdgeOverflow" : false});
        }
        {
            var Q0;
            Q0=makeQuery(id+"F1.opExtrude","SWEPT_EDGE",EDGE,{"disambiguationData":[OSD([sQuery(id+"F0.wireOp",EDGE,"E46.bottom"),sQuery(id+"F0.wireOp",EDGE,"E46.left"),sQuery(id+"F0.wireOp",EDGE,"E47.bottom"),sQuery(id+"F0.wireOp",EDGE,"E47.left"),sQuery(id+"F0.wireOp",EDGE,"E49")])]});
            var Q1;
            Q1=makeQuery(id+"F1.opExtrude","SWEPT_EDGE",EDGE,{"disambiguationData":[OSD([sQuery(id+"F0.wireOp",EDGE,"E46.bottom"),sQuery(id+"F0.wireOp",EDGE,"E46.right")])]});
            fillet(context, id + "F3", {"entities" : qUnion([Q0, Q1]), "radius" : 5.08 * mm, "tangentPropagation" : true, "allowEdgeOverflow" : false});
        }
        {
            var Q0;
            Q0=makeQuery(id+"F1.opExtrude","SWEPT_EDGE",EDGE,{"disambiguationData":[OSD([sQuery(id+"F0.wireOp",EDGE,"E0.top"),sQuery(id+"F0.wireOp",EDGE,"E46.top"),sQuery(id+"F0.wireOp",EDGE,"E46.right")])]});
            fillet(context, id + "F4", {"entities" : qUnion([Q0]), "radius" : 5.08 * mm, "tangentPropagation" : true, "allowEdgeOverflow" : false});
        }
        {
            var Q0;
            Q0=makeQuery(id+"F1.opExtrude","SWEPT_EDGE",EDGE,{"disambiguationData":[OSD([sQuery(id+"F0.wireOp",EDGE,"E47.top"),sQuery(id+"F0.wireOp",EDGE,"E47.right")])]});
            fillet(context, id + "F5", {"entities" : qUnion([Q0]), "radius" : 5.08 * mm, "tangentPropagation" : true, "allowEdgeOverflow" : false});
        }
        {
            var Q0;
            Q0=makeQuery(id+"F1.opExtrude","SWEPT_EDGE",EDGE,{"disambiguationData":[OSD([sQuery(id+"F0.wireOp",EDGE,"E47.right"),sQuery(id+"F0.wireOp",EDGE,"E49")])]});
            fillet(context, id + "F6", {"entities" : qUnion([Q0]), "radius" : 5.08 * mm, "tangentPropagation" : true, "allowEdgeOverflow" : false});
        }
        {
            var Q0;
            Q0=makeQuery(id+"F1.opExtrude","SWEPT_EDGE",EDGE,{"disambiguationData":[OSD([sQuery(id+"F0.wireOp",EDGE,"E1.bottom"),sQuery(id+"F0.wireOp",EDGE,"E1.right")])]});
            fillet(context, id + "F7", {"entities" : qUnion([Q0]), "radius" : 5.08 * mm, "tangentPropagation" : true, "allowEdgeOverflow" : false});
        }
        {
            var Q0;
            Q0=makeQuery(id+"F1.opExtrude","SWEPT_EDGE",EDGE,{"disambiguationData":[OSD([sQuery(id+"F0.wireOp",EDGE,"E1.top"),sQuery(id+"F0.wireOp",EDGE,"E1.right"),sQuery(id+"F0.wireOp",EDGE,"E54")])]});
            fillet(context, id + "F8", {"entities" : qUnion([Q0]), "radius" : 5.08 * mm, "tangentPropagation" : true, "allowEdgeOverflow" : false});
        }
        {
            var Q0;
            Q0=makeQuery(id+"F1.opExtrude","SWEPT_EDGE",EDGE,{"disambiguationData":[OSD([sQuery(id+"F0.wireOp",EDGE,"E50.bottom"),sQuery(id+"F0.wireOp",EDGE,"E50.right"),sQuery(id+"F0.wireOp",EDGE,"E54")])]});
            fillet(context, id + "F9", {"entities" : qUnion([Q0]), "radius" : 5.08 * mm, "tangentPropagation" : true, "allowEdgeOverflow" : false});
        }
    });
